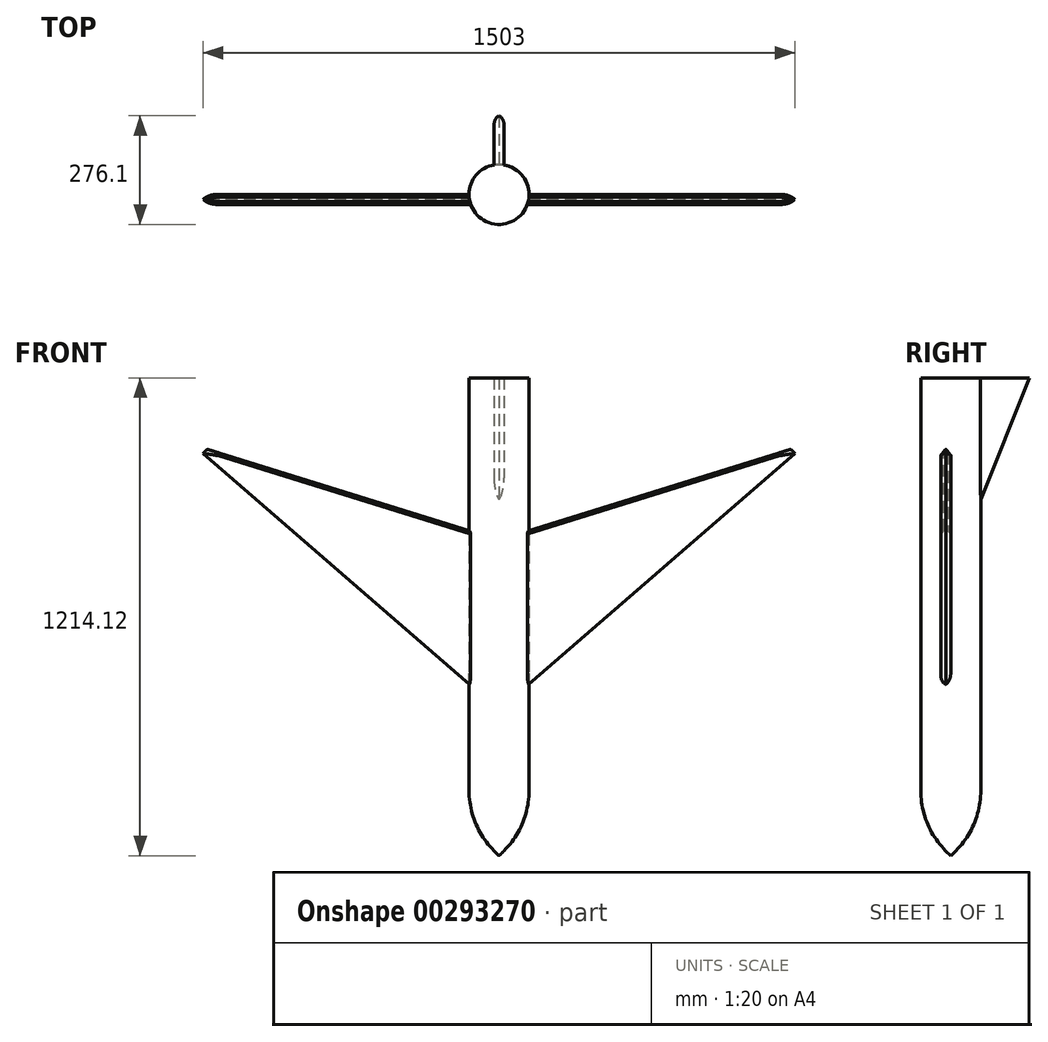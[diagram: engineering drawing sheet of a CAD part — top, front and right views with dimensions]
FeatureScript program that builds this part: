
annotation { "Feature Type Name" : "Feature", "Feature Type Description" : "" }
export const myFeature = defineFeature(function(context is Context, id is Id, definition is map)
    precondition{}
    {
        {
            var Q0;
            Q0=qCreatedBy(makeId("Top.planeOp"),FACE);
            var sketch = newSketch(context, id + "F0", { "sketchPlane" : qUnion([Q0])});
            skCircle(sketch, "E0", {"center": v(0, 0) * mm, "radius": 76.2 * mm});
            skLineSegment(sketch, "E1", {"start": v(0, 0) * mm, "end": v(-17.57, 0) * mm});
            skSolve(sketch);
        }
        {
            var Q0;
            Q0 = qSketchRegion(id + "F0", true);
            extrude(context, id + "F1", {"entities" : qUnion([Q0]), "endBound" : BoundingType.SYMMETRIC, "depth" : 1016 * mm});
        }
        {
            var Q0;
            Q0=qCreatedBy(makeId("Front.planeOp"),FACE);
            var sketch = newSketch(context, id + "F2", { "sketchPlane" : qUnion([Q0])});
            skLineSegment(sketch, "E2", {"start": v(0, -899.38) * mm, "end": v(0, 733.1) * mm});
            skPoint(sketch, "E3.middle", {"position": v(0, 0) * mm});
            skLineSegment(sketch, "E4", {"start": v(0, -339.26) * mm, "end": v(-781.47, 339.26) * mm});
            skLineSegment(sketch, "E5", {"start": v(0, -339.26) * mm, "end": v(781.47, 339.26) * mm});
            skLineSegment(sketch, "E6", {"start": v(-781.47, 339.26) * mm, "end": v(0, 96.4) * mm});
            skLineSegment(sketch, "E7", {"start": v(0, 96.4) * mm, "end": v(781.47, 339.26) * mm});
            skSolve(sketch);
        }
        {
            var Q0;
            Q0 = qSketchRegion(id + "F2", true);
            extrude(context, id + "F3", {"entities" : qUnion([Q0]), "operationType" : NewBodyOperationType.ADD, "depth" : 25.4 * mm});
        }
        {
            var Q0;
            Q0=makeQuery(id+"F3.opExtrude","CAP_EDGE",EDGE,{"disambiguationData":[OSD([sQuery(id+"F2.wireOp",EDGE,"E4")])],"isStart":true});
            var Q1;
            Q1=makeQuery(id+"F3.opExtrude","CAP_EDGE",EDGE,{"disambiguationData":[OSD([sQuery(id+"F2.wireOp",EDGE,"E4")])],"isStart":false});
            fillet(context, id + "F4", {"entities" : qUnion([Q0, Q1]), "radius" : 22.86 * mm, "tangentPropagation" : true, "allowEdgeOverflow" : false});
        }
        {
            var Q0;
            Q0=makeQuery(id+"F3.opExtrude","CAP_EDGE",EDGE,{"disambiguationData":[OSD([sQuery(id+"F2.wireOp",EDGE,"E5")])],"isStart":true});
            var Q1;
            Q1=makeQuery(id+"F3.opExtrude","CAP_EDGE",EDGE,{"disambiguationData":[OSD([sQuery(id+"F2.wireOp",EDGE,"E5")])],"isStart":false});
            fillet(context, id + "F5", {"entities" : qUnion([Q0, Q1]), "radius" : 22.86 * mm, "tangentPropagation" : true, "allowEdgeOverflow" : false});
        }
        {
            var Q0;
            Q0=makeQuery(id+"F3.opExtrude","CAP_EDGE",EDGE,{"disambiguationData":[OSD([sQuery(id+"F2.wireOp",EDGE,"E7")])],"isStart":true});
            var Q1;
            Q1=makeQuery(id+"F3.opExtrude","CAP_EDGE",EDGE,{"disambiguationData":[OSD([sQuery(id+"F2.wireOp",EDGE,"E7")])],"isStart":false});
            var Q2;
            Q2=makeQuery(id+"F3.opExtrude","CAP_EDGE",EDGE,{"disambiguationData":[OSD([sQuery(id+"F2.wireOp",EDGE,"E6")])],"isStart":true});
            var Q3;
            Q3=makeQuery(id+"F3.opExtrude","CAP_EDGE",EDGE,{"disambiguationData":[OSD([sQuery(id+"F2.wireOp",EDGE,"E6")])],"isStart":false});
            chamfer(context, id + "F6", {"entities" : qUnion([Q0, Q1, Q2, Q3]), "width" : 7.11 * mm, "tangentPropagation" : true});
        }
        {
            var Q0;
            Q0=qCreatedBy(makeId("Right.planeOp"),FACE);
            var sketch = newSketch(context, id + "F7", { "sketchPlane" : qUnion([Q0])});
            skPoint(sketch, "E8.middle", {"position": v(0, 0) * mm});
            skLineSegment(sketch, "E9.top", {"start": v(0, 508) * mm, "end": v(203.17, 508) * mm});
            skLineSegment(sketch, "E9.left", {"start": v(0, 0) * mm, "end": v(0, 508) * mm});
            skLineSegment(sketch, "E10", {"start": v(0, 0) * mm, "end": v(203.17, 508) * mm});
            skLineSegment(sketch, "E11", {"start": v(0, 508) * mm, "end": v(0, 0) * mm});
            skLineSegment(sketch, "E12", {"start": v(1.06, 508) * mm, "end": v(-1.18, 508) * mm});
            skSolve(sketch);
        }
        {
            var Q0;
            Q0 = qSketchRegion(id + "F7", true);
            extrude(context, id + "F8", {"entities" : qUnion([Q0]), "operationType" : NewBodyOperationType.ADD, "endBound" : BoundingType.SYMMETRIC, "depth" : 25.4 * mm});
        }
        {
            var Q0;
            Q0=makeQuery(id+"F8.opExtrude","CAP_EDGE",EDGE,{"disambiguationData":[OSD([sQuery(id+"F7.wireOp",EDGE,"E10")])],"isStart":false});
            var Q1;
            Q1=makeQuery(id+"F8.opExtrude","CAP_EDGE",EDGE,{"disambiguationData":[OSD([sQuery(id+"F7.wireOp",EDGE,"E10")])],"isStart":true});
            fillet(context, id + "F9", {"entities" : qUnion([Q0, Q1]), "radius" : 24.53 * mm, "tangentPropagation" : true, "allowEdgeOverflow" : false});
        }
        {
            var Q0;
            Q0=makeQuery(id+"F1.opExtrude","CAP_FACE",FACE,{"disambiguationData":[OSD([sQuery(id+"F0.wireOp",EDGE,"E0")])],"isStart":true});
            var sketch = newSketch(context, id + "F10", { "sketchPlane" : qUnion([Q0])});
            skCircle(sketch, "E13", {"center": v(0, 0) * mm, "radius": 76.2 * mm});
            skSolve(sketch);
        }
        {
            var Q0;
            Q0 = qSketchRegion(id + "F10", true);
            extrude(context, id + "F11", {"entities" : qUnion([Q0]), "operationType" : NewBodyOperationType.ADD, "depth" : 198.12 * mm});
        }
        {
            var Q0;
            Q0=makeQuery(id+"F11.opExtrude","CAP_EDGE",EDGE,{"disambiguationData":[OSD([sQuery(id+"F10.wireOp",EDGE,"E13")])],"isStart":false});
            chamfer(context, id + "F12", {"entities" : qUnion([Q0]), "width" : 76.2 * mm, "tangentPropagation" : true});
        }
        {
            var Q0;
            Q0=makeQuery(id+"F12.opChamfer","BLEND_FACE",FACE,{"disambiguationData":[OSD([sQuery(id+"F10.wireOp",EDGE,"E13")])]});
            fillet(context, id + "F13", {"entities" : qUnion([Q0]), "radius" : 215.8 * mm, "tangentPropagation" : true, "allowEdgeOverflow" : false});
        }
    });
